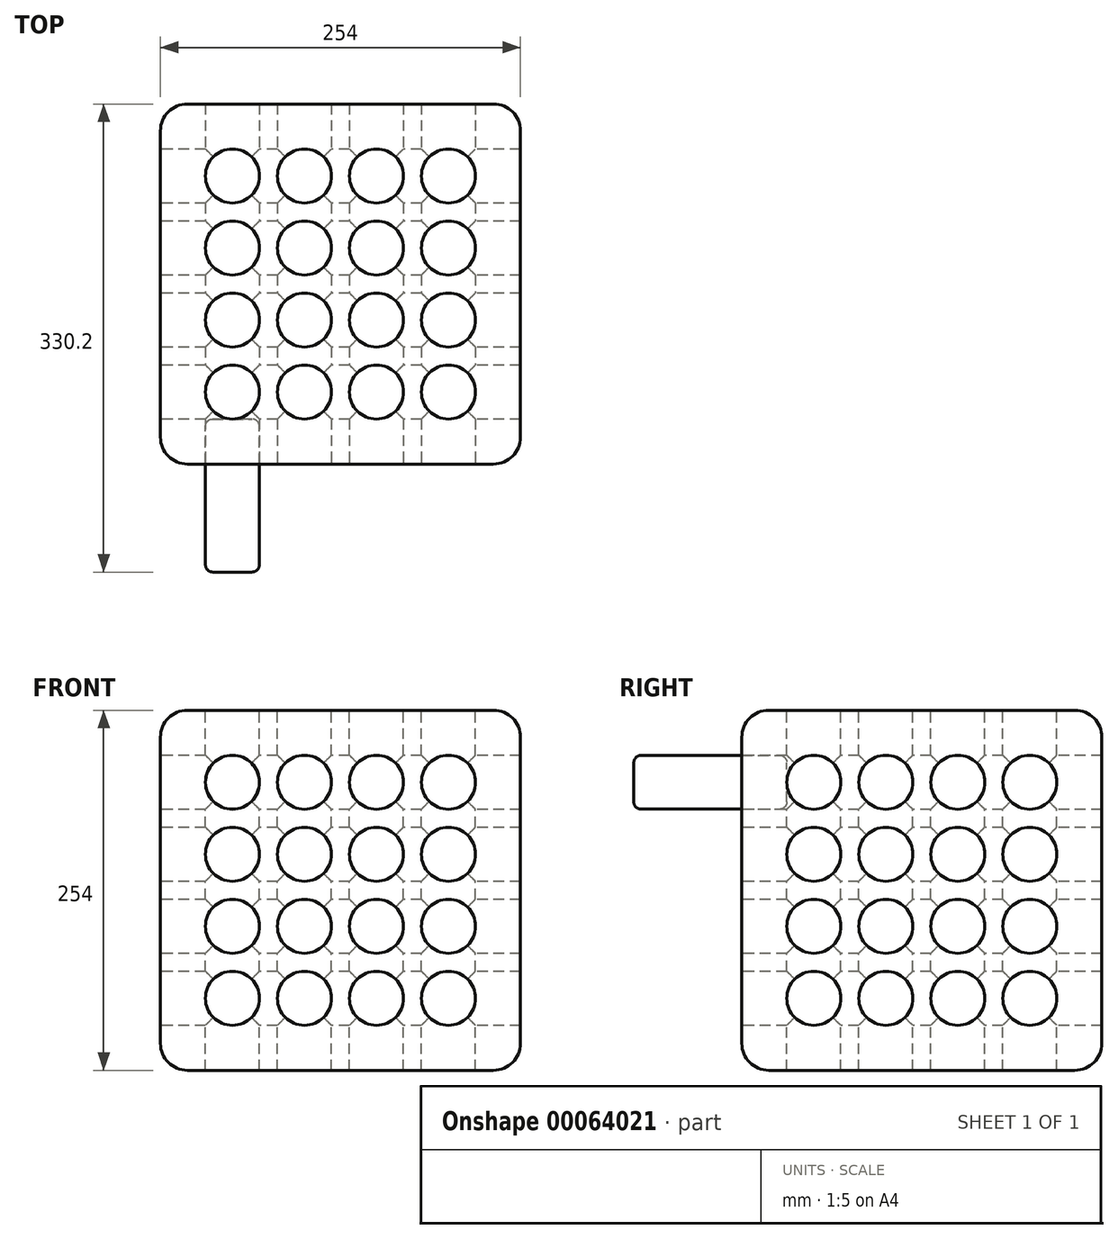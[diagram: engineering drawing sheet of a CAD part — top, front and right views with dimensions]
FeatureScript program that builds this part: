
annotation { "Feature Type Name" : "Feature", "Feature Type Description" : "" }
export const myFeature = defineFeature(function(context is Context, id is Id, definition is map)
    precondition{}
    {
        {
            var Q0;
            Q0=qCreatedBy(makeId("Top.planeOp"),FACE);
            var sketch = newSketch(context, id + "F0", { "sketchPlane" : qUnion([Q0])});
            skLineSegment(sketch, "E0.bottom", {"start": v(0, 0) * mm, "end": v(254, 0) * mm});
            skLineSegment(sketch, "E0.top", {"start": v(0, 254) * mm, "end": v(254, 254) * mm});
            skLineSegment(sketch, "E0.left", {"start": v(0, 0) * mm, "end": v(0, 254) * mm});
            skLineSegment(sketch, "E0.right", {"start": v(254, 0) * mm, "end": v(254, 254) * mm});
            skSolve(sketch);
        }
        {
            var Q0;
            Q0 = qSketchRegion(id + "F0", true);
            extrude(context, id + "F1", {"entities" : qUnion([Q0]), "depth" : 254 * mm});
        }
        {
            var Q0;
            Q0=makeQuery(id+"F1.opExtrude","CAP_FACE",FACE,{"disambiguationData":[OSD([sQuery(id+"F0.wireOp",EDGE,"E0.bottom"),sQuery(id+"F0.wireOp",EDGE,"E0.top"),sQuery(id+"F0.wireOp",EDGE,"E0.left"),sQuery(id+"F0.wireOp",EDGE,"E0.right")])],"isStart":false});
            var sketch = newSketch(context, id + "F2", { "sketchPlane" : qUnion([Q0])});
            skCircle(sketch, "E1", {"center": v(50.8, 50.8) * mm, "radius": 19.05 * mm});
            skCircle(sketch, "E2.0.1.0", {"center": v(50.8, 101.6) * mm, "radius": 19.05 * mm});
            skCircle(sketch, "E2.0.2.0", {"center": v(50.8, 152.4) * mm, "radius": 19.05 * mm});
            skCircle(sketch, "E2.0.3.0", {"center": v(50.8, 203.2) * mm, "radius": 19.05 * mm});
            skCircle(sketch, "E2.1.0.0", {"center": v(101.6, 50.8) * mm, "radius": 19.05 * mm});
            skCircle(sketch, "E2.1.1.0", {"center": v(101.6, 101.6) * mm, "radius": 19.05 * mm});
            skCircle(sketch, "E2.1.2.0", {"center": v(101.6, 152.4) * mm, "radius": 19.05 * mm});
            skCircle(sketch, "E2.1.3.0", {"center": v(101.6, 203.2) * mm, "radius": 19.05 * mm});
            skCircle(sketch, "E2.2.0.0", {"center": v(152.4, 50.8) * mm, "radius": 19.05 * mm});
            skCircle(sketch, "E2.2.1.0", {"center": v(152.4, 101.6) * mm, "radius": 19.05 * mm});
            skCircle(sketch, "E2.2.2.0", {"center": v(152.4, 152.4) * mm, "radius": 19.05 * mm});
            skCircle(sketch, "E2.2.3.0", {"center": v(152.4, 203.2) * mm, "radius": 19.05 * mm});
            skCircle(sketch, "E2.3.0.0", {"center": v(203.2, 50.8) * mm, "radius": 19.05 * mm});
            skCircle(sketch, "E2.3.1.0", {"center": v(203.2, 101.6) * mm, "radius": 19.05 * mm});
            skCircle(sketch, "E2.3.2.0", {"center": v(203.2, 152.4) * mm, "radius": 19.05 * mm});
            skCircle(sketch, "E2.3.3.0", {"center": v(203.2, 203.2) * mm, "radius": 19.05 * mm});
            skLineSegment(sketch, "E2.direction1", {"start": v(50.8, 50.8) * mm, "end": v(101.6, 50.8) * mm, "construction": true});
            skLineSegment(sketch, "E2.direction2", {"start": v(50.8, 50.8) * mm, "end": v(50.8, 101.6) * mm, "construction": true});
            skSolve(sketch);
        }
        {
            var Q0;
            Q0=makeQuery(id+"F1.opExtrude","SWEPT_FACE",FACE,{"disambiguationData":[OSD([sQuery(id+"F0.wireOp",EDGE,"E0.bottom")])]});
            var sketch = newSketch(context, id + "F3", { "sketchPlane" : qUnion([Q0])});
            skCircle(sketch, "E3", {"center": v(50.8, 50.8) * mm, "radius": 19.05 * mm});
            skCircle(sketch, "E4.0.1.0", {"center": v(50.8, 101.6) * mm, "radius": 19.05 * mm});
            skCircle(sketch, "E4.0.2.0", {"center": v(50.8, 152.4) * mm, "radius": 19.05 * mm});
            skCircle(sketch, "E4.0.3.0", {"center": v(50.8, 203.2) * mm, "radius": 19.05 * mm});
            skCircle(sketch, "E4.1.0.0", {"center": v(101.6, 50.8) * mm, "radius": 19.05 * mm});
            skCircle(sketch, "E4.1.1.0", {"center": v(101.6, 101.6) * mm, "radius": 19.05 * mm});
            skCircle(sketch, "E4.1.2.0", {"center": v(101.6, 152.4) * mm, "radius": 19.05 * mm});
            skCircle(sketch, "E4.1.3.0", {"center": v(101.6, 203.2) * mm, "radius": 19.05 * mm});
            skCircle(sketch, "E4.2.0.0", {"center": v(152.4, 50.8) * mm, "radius": 19.05 * mm});
            skCircle(sketch, "E4.2.1.0", {"center": v(152.4, 101.6) * mm, "radius": 19.05 * mm});
            skCircle(sketch, "E4.2.2.0", {"center": v(152.4, 152.4) * mm, "radius": 19.05 * mm});
            skCircle(sketch, "E4.2.3.0", {"center": v(152.4, 203.2) * mm, "radius": 19.05 * mm});
            skCircle(sketch, "E4.3.0.0", {"center": v(203.2, 50.8) * mm, "radius": 19.05 * mm});
            skCircle(sketch, "E4.3.1.0", {"center": v(203.2, 101.6) * mm, "radius": 19.05 * mm});
            skCircle(sketch, "E4.3.2.0", {"center": v(203.2, 152.4) * mm, "radius": 19.05 * mm});
            skCircle(sketch, "E4.3.3.0", {"center": v(203.2, 203.2) * mm, "radius": 19.05 * mm});
            skLineSegment(sketch, "E4.direction1", {"start": v(50.8, 50.8) * mm, "end": v(101.6, 50.8) * mm, "construction": true});
            skLineSegment(sketch, "E4.direction2", {"start": v(50.8, 50.8) * mm, "end": v(50.8, 101.6) * mm, "construction": true});
            skSolve(sketch);
        }
        {
            var Q0;
            Q0=makeQuery(id+"F1.opExtrude","SWEPT_FACE",FACE,{"disambiguationData":[OSD([sQuery(id+"F0.wireOp",EDGE,"E0.left")])]});
            var sketch = newSketch(context, id + "F4", { "sketchPlane" : qUnion([Q0])});
            skCircle(sketch, "E5", {"center": v(-50.8, 50.8) * mm, "radius": 19.05 * mm});
            skCircle(sketch, "E6.0.1.0", {"center": v(-50.8, 101.6) * mm, "radius": 19.05 * mm});
            skCircle(sketch, "E6.0.2.0", {"center": v(-50.8, 152.4) * mm, "radius": 19.05 * mm});
            skCircle(sketch, "E6.0.3.0", {"center": v(-50.8, 203.2) * mm, "radius": 19.05 * mm});
            skCircle(sketch, "E6.1.0.0", {"center": v(-101.6, 50.8) * mm, "radius": 19.05 * mm});
            skCircle(sketch, "E6.1.1.0", {"center": v(-101.6, 101.6) * mm, "radius": 19.05 * mm});
            skCircle(sketch, "E6.1.2.0", {"center": v(-101.6, 152.4) * mm, "radius": 19.05 * mm});
            skCircle(sketch, "E6.1.3.0", {"center": v(-101.6, 203.2) * mm, "radius": 19.05 * mm});
            skCircle(sketch, "E6.2.0.0", {"center": v(-152.4, 50.8) * mm, "radius": 19.05 * mm});
            skCircle(sketch, "E6.2.1.0", {"center": v(-152.4, 101.6) * mm, "radius": 19.05 * mm});
            skCircle(sketch, "E6.2.2.0", {"center": v(-152.4, 152.4) * mm, "radius": 19.05 * mm});
            skCircle(sketch, "E6.2.3.0", {"center": v(-152.4, 203.2) * mm, "radius": 19.05 * mm});
            skCircle(sketch, "E6.3.0.0", {"center": v(-203.2, 50.8) * mm, "radius": 19.05 * mm});
            skCircle(sketch, "E6.3.1.0", {"center": v(-203.2, 101.6) * mm, "radius": 19.05 * mm});
            skCircle(sketch, "E6.3.2.0", {"center": v(-203.2, 152.4) * mm, "radius": 19.05 * mm});
            skCircle(sketch, "E6.3.3.0", {"center": v(-203.2, 203.2) * mm, "radius": 19.05 * mm});
            skLineSegment(sketch, "E6.direction1", {"start": v(-50.8, 50.8) * mm, "end": v(-101.6, 50.8) * mm, "construction": true});
            skLineSegment(sketch, "E6.direction2", {"start": v(-50.8, 50.8) * mm, "end": v(-50.8, 101.6) * mm, "construction": true});
            skSolve(sketch);
        }
        {
            var Q0;
            Q0 = qSketchRegion(id + "F2", true);
            extrude(context, id + "F5", {"entities" : qUnion([Q0]), "operationType" : NewBodyOperationType.REMOVE, "endBound" : BoundingType.THROUGH_ALL, "oppositeDirection" : true, "depth" : 25.4 * mm});
        }
        {
            var Q0;
            Q0 = qSketchRegion(id + "F3", true);
            extrude(context, id + "F6", {"entities" : qUnion([Q0]), "operationType" : NewBodyOperationType.REMOVE, "endBound" : BoundingType.THROUGH_ALL, "oppositeDirection" : true, "depth" : 25.4 * mm});
        }
        {
            var Q0;
            Q0 = qSketchRegion(id + "F4", true);
            extrude(context, id + "F7", {"entities" : qUnion([Q0]), "operationType" : NewBodyOperationType.REMOVE, "endBound" : BoundingType.THROUGH_ALL, "oppositeDirection" : true, "depth" : 25.4 * mm});
        }
        {
            var Q0;
            Q0=makeQuery(id+"F1.opExtrude","SWEPT_FACE",FACE,{"disambiguationData":[OSD([sQuery(id+"F0.wireOp",EDGE,"E0.bottom")])]});
            var sketch = newSketch(context, id + "F8", { "sketchPlane" : qUnion([Q0])});
            skCircle(sketch, "E7", {"center": v(50.8, 203.2) * mm, "radius": 18.99 * mm});
            skSolve(sketch);
        }
        {
            var Q0;
            Q0 = qSketchRegion(id + "F8", true);
            extrude(context, id + "F9", {"entities" : qUnion([Q0]), "depth" : 76.2 * mm, "hasSecondDirection" : true, "secondDirectionOppositeDirection" : true, "secondDirectionDepth" : 31.75 * mm});
        }
        {
            var Q0;
            Q0=makeQuery(id+"F9.opExtrude","CAP_EDGE",EDGE,{"disambiguationData":[OSD([sQuery(id+"F8.wireOp",EDGE,"E7")])],"isStart":false});
            var Q1;
            Q1=makeQuery(id+"F9.opExtrude","CAP_EDGE",EDGE,{"disambiguationData":[OSD([sQuery(id+"F8.wireOp",EDGE,"E7")])],"isStart":true});
            fillet(context, id + "F10", {"entities" : qUnion([Q0, Q1]), "radius" : 5.08 * mm, "tangentPropagation" : true, "allowEdgeOverflow" : false});
        }
        {
            var Q0;
            Q0=makeQuery(id+"F1.opExtrude","CAP_EDGE",EDGE,{"disambiguationData":[OSD([sQuery(id+"F0.wireOp",EDGE,"E0.bottom")])],"isStart":false});
            var Q1;
            Q1=makeQuery(id+"F1.opExtrude","CAP_EDGE",EDGE,{"disambiguationData":[OSD([sQuery(id+"F0.wireOp",EDGE,"E0.left")])],"isStart":false});
            var Q2;
            Q2=makeQuery(id+"F1.opExtrude","SWEPT_EDGE",EDGE,{"disambiguationData":[OSD([sQuery(id+"F0.wireOp",EDGE,"E0.bottom"),sQuery(id+"F0.wireOp",EDGE,"E0.left")])]});
            var Q3;
            Q3=makeQuery(id+"F1.opExtrude","SWEPT_EDGE",EDGE,{"disambiguationData":[OSD([sQuery(id+"F0.wireOp",EDGE,"E0.top"),sQuery(id+"F0.wireOp",EDGE,"E0.left")])]});
            var Q4;
            Q4=makeQuery(id+"F1.opExtrude","CAP_EDGE",EDGE,{"disambiguationData":[OSD([sQuery(id+"F0.wireOp",EDGE,"E0.left")])],"isStart":true});
            var Q5;
            Q5=makeQuery(id+"F1.opExtrude","CAP_EDGE",EDGE,{"disambiguationData":[OSD([sQuery(id+"F0.wireOp",EDGE,"E0.bottom")])],"isStart":true});
            var Q6;
            Q6=makeQuery(id+"F1.opExtrude","SWEPT_EDGE",EDGE,{"disambiguationData":[OSD([sQuery(id+"F0.wireOp",EDGE,"E0.bottom"),sQuery(id+"F0.wireOp",EDGE,"E0.right")])]});
            var Q7;
            Q7=makeQuery(id+"F1.opExtrude","CAP_EDGE",EDGE,{"disambiguationData":[OSD([sQuery(id+"F0.wireOp",EDGE,"E0.right")])],"isStart":false});
            var Q8;
            Q8=makeQuery(id+"F1.opExtrude","CAP_EDGE",EDGE,{"disambiguationData":[OSD([sQuery(id+"F0.wireOp",EDGE,"E0.top")])],"isStart":false});
            var Q9;
            Q9=makeQuery(id+"F1.opExtrude","CAP_EDGE",EDGE,{"disambiguationData":[OSD([sQuery(id+"F0.wireOp",EDGE,"E0.right")])],"isStart":true});
            var Q10;
            Q10=makeQuery(id+"F1.opExtrude","SWEPT_EDGE",EDGE,{"disambiguationData":[OSD([sQuery(id+"F0.wireOp",EDGE,"E0.top"),sQuery(id+"F0.wireOp",EDGE,"E0.right")])]});
            var Q11;
            Q11=makeQuery(id+"F1.opExtrude","CAP_EDGE",EDGE,{"disambiguationData":[OSD([sQuery(id+"F0.wireOp",EDGE,"E0.top")])],"isStart":true});
            fillet(context, id + "F11", {"entities" : qUnion([Q0, Q1, Q2, Q3, Q4, Q5, Q6, Q7, Q8, Q9, Q10, Q11]), "radius" : 19.05 * mm, "tangentPropagation" : true, "allowEdgeOverflow" : false});
        }
    });
